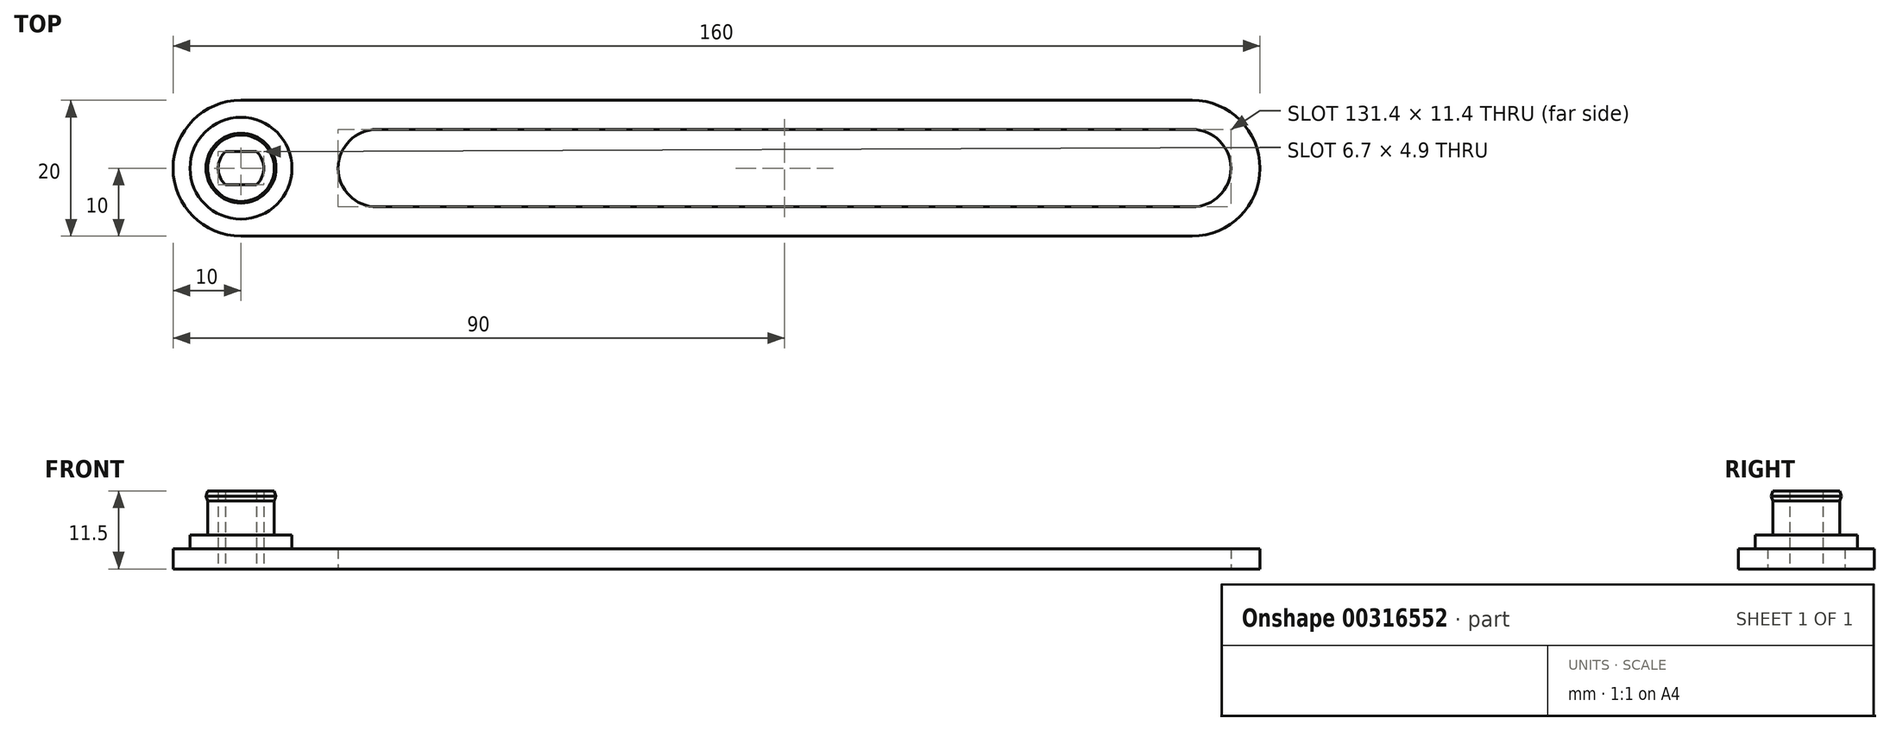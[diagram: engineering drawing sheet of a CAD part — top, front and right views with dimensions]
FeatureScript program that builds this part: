
annotation { "Feature Type Name" : "Feature", "Feature Type Description" : "" }
export const myFeature = defineFeature(function(context is Context, id is Id, definition is map)
    precondition{}
    {
        {
            assignVariable(context, id + "F0", {"name" : "e", "anyValue" : 3});
        }
        {
            var Q0;
            Q0=qCreatedBy(makeId("Top.planeOp"),FACE);
            var sketch = newSketch(context, id + "F1", { "sketchPlane" : qUnion([Q0])});
            skLineSegment(sketch, "E0.bottom", {"start": v(0, 10) * mm, "end": v(120, 10) * mm});
            skLineSegment(sketch, "E0.top", {"start": v(0, -10) * mm, "end": v(120, -10) * mm});
            skPoint(sketch, "E1", {"position": v(-14.5, 0) * mm});
            skPoint(sketch, "E2.visualSharp", {"position": v(134.5, 10) * mm});
            skPoint(sketch, "E3.visualSharp", {"position": v(134.5, -10) * mm});
            skPoint(sketch, "E4.visualSharp", {"position": v(-14.5, -10) * mm});
            skPoint(sketch, "E5.visualSharp", {"position": v(-14.5, 10) * mm});
            skPoint(sketch, "E6", {"position": v(20, 0) * mm});
            skLineSegment(sketch, "E7.bottom", {"start": v(20, 5.7) * mm, "end": v(120, 5.7) * mm});
            skLineSegment(sketch, "E7.top", {"start": v(20, -5.7) * mm, "end": v(120, -5.7) * mm});
            skLineSegment(sketch, "E7.left", {"start": v(20, 5.7) * mm, "end": v(20, -5.7) * mm, "construction": true});
            skArc(sketch, "E8", {"start": v(20, 5.7) * mm, "mid": v(14.3, 0) * mm, "end": v(20, -5.7) * mm});
            skCircle(sketch, "E9", {"center": v(0, 0) * mm, "radius": 7.5 * mm});
            skLineSegment(sketch, "E10", {"start": v(0, 0) * mm, "end": v(0, -2.45) * mm, "construction": true});
            skLineSegment(sketch, "E11", {"start": v(0, 0) * mm, "end": v(0, 2.45) * mm, "construction": true});
            skCircle(sketch, "E12", {"center": v(0, 0) * mm, "radius": 3.35 * mm, "construction": true});
            skLineSegment(sketch, "E13", {"start": v(0, -2.45) * mm, "end": v(-2.28, -2.45) * mm});
            skLineSegment(sketch, "E14", {"start": v(0, -2.45) * mm, "end": v(2.28, -2.45) * mm});
            skLineSegment(sketch, "E15", {"start": v(0, 2.45) * mm, "end": v(2.28, 2.45) * mm});
            skLineSegment(sketch, "E16", {"start": v(0, 2.45) * mm, "end": v(-2.28, 2.45) * mm});
            skArc(sketch, "E17", {"start": v(-2.28, -2.45) * mm, "mid": v(-3.35, 0) * mm, "end": v(-2.28, 2.45) * mm});
            skArc(sketch, "E18", {"start": v(2.28, -2.45) * mm, "mid": v(3.35, 0) * mm, "end": v(2.28, 2.45) * mm});
            skCircle(sketch, "E19", {"center": v(0, 0) * mm, "radius": 4.9 * mm});
            skPoint(sketch, "E2.filletArc.center.orphan", {"position": v(120, -4.5) * mm});
            skArc(sketch, "E20", {"start": v(0, 10) * mm, "mid": v(-10, 0) * mm, "end": v(0, -10) * mm});
            skLineSegment(sketch, "E21", {"start": v(120, 10) * mm, "end": v(120, -10) * mm, "construction": true});
            skPoint(sketch, "E22", {"position": v(120, 0) * mm});
            skLineSegment(sketch, "E23", {"start": v(120, 5.7) * mm, "end": v(140, 5.7) * mm});
            skLineSegment(sketch, "E24", {"start": v(120, -5.7) * mm, "end": v(140, -5.7) * mm});
            skLineSegment(sketch, "E25", {"start": v(120, 10) * mm, "end": v(140, 10) * mm});
            skLineSegment(sketch, "E26", {"start": v(120, -10) * mm, "end": v(140, -10) * mm});
            skArc(sketch, "E27", {"start": v(140, 5.7) * mm, "mid": v(145.7, 0) * mm, "end": v(140, -5.7) * mm});
            skArc(sketch, "E28", {"start": v(140, 10) * mm, "mid": v(150, 0) * mm, "end": v(140, -10) * mm});
            skSolve(sketch);
        }
        {
            var Q0;
            Q0=makeQuery(id+"F1.imprint","IMPRINT",FACE,{"disambiguationData":[TD([[makeQuery(id+"F1.imprint","IMPRINT",EDGE,{"derivedFrom":sQuery(id+"F1.wireOp",EDGE,"E0.bottom")}),-1.0]])]});
            var Q1;
            Q1=makeQuery(id+"F1.imprint","IMPRINT",FACE,{"disambiguationData":[TD([[makeQuery(id+"F1.imprint","IMPRINT",EDGE,{"derivedFrom":sQuery(id+"F1.wireOp",EDGE,"IskUjNax-6XSr-Ja0F-QV4T-S56PLot7pUtS")}),-1.0]])]});
            extrude(context, id + "F2", {"entities" : qUnion([Q0, Q1]), "depth" : (getVariable(context, 'e')) * mm});
        }
        {
            var Q0;
            Q0=makeQuery(id+"F1.imprint","IMPRINT",FACE,{"disambiguationData":[TD([[makeQuery(id+"F1.imprint","IMPRINT",EDGE,{"derivedFrom":sQuery(id+"F1.wireOp",EDGE,"E9")}),1.0]])]});
            extrude(context, id + "F3", {"entities" : qUnion([Q0]), "operationType" : NewBodyOperationType.ADD, "depth" : 5 * mm});
        }
        {
            var Q0;
            Q0=makeQuery(id+"F1.imprint","IMPRINT",FACE,{"disambiguationData":[TD([[makeQuery(id+"F1.imprint","IMPRINT",EDGE,{"derivedFrom":sQuery(id+"F1.wireOp",EDGE,"E13")}),1.0]])]});
            extrude(context, id + "F4", {"entities" : qUnion([Q0]), "operationType" : NewBodyOperationType.ADD, "depth" : 11.5 * mm});
        }
        {
            var Q0;
            Q0=sQuery(id+"F1.wireOp",VERTEX,"E11.start");
            var Q1;
            Q1=makeQuery(id+"F4.opExtrude","SWEPT_FACE",FACE,{"disambiguationData":[OSD([sQuery(id+"F1.wireOp",EDGE,"E15"),sQuery(id+"F1.wireOp",EDGE,"E16")])]});
            cPlane(context, id + "F5", {"entities" : qUnion([Q0, Q1]), "cplaneType" : CPlaneType.PLANE_POINT, "offset" : 25 * mm, "width" : 150 * mm, "height" : 150 * mm});
        }
        {
            var Q0;
            Q0=qCreatedBy(id+"F5.planeOp",FACE);
            var sketch = newSketch(context, id + "F6", { "sketchPlane" : qUnion([Q0])});
            skPoint(sketch, "E29.0", {"position": v(0, 0) * mm});
            skLineSegment(sketch, "E30.0", {"start": v(-4.9, 11.5) * mm, "end": v(4.9, 11.5) * mm});
            skLineSegment(sketch, "E31", {"start": v(0, 0) * mm, "end": v(0, 11.5) * mm});
            skLineSegment(sketch, "E32", {"start": v(4.9, 11.5) * mm, "end": v(4.9, 10) * mm});
            skLineSegment(sketch, "E33", {"start": v(4.9, 10.75) * mm, "end": v(5.15, 10.75) * mm, "construction": true});
            skLineSegment(sketch, "E34", {"start": v(5.15, 10.75) * mm, "end": v(4.9, 11.5) * mm});
            skLineSegment(sketch, "E35", {"start": v(5.15, 10.75) * mm, "end": v(4.9, 10) * mm});
            skSolve(sketch);
        }
        {
            var Q0;
            Q0=makeQuery(id+"F6.imprint","IMPRINT",FACE,{"disambiguationData":[TD([[makeQuery(id+"F6.imprint","IMPRINT",EDGE,{"derivedFrom":sQuery(id+"F6.wireOp",EDGE,"E32")}),1.0]])]});
            var Q1;
            Q1=sQuery(id+"F6.wireOp",EDGE,"E31");
            revolve(context, id + "F7", {"operationType" : NewBodyOperationType.ADD, "entities" : qUnion([Q0]), "axis" : qUnion([Q1]), "revolveType" : RevolveType.FULL});
        }
    });
